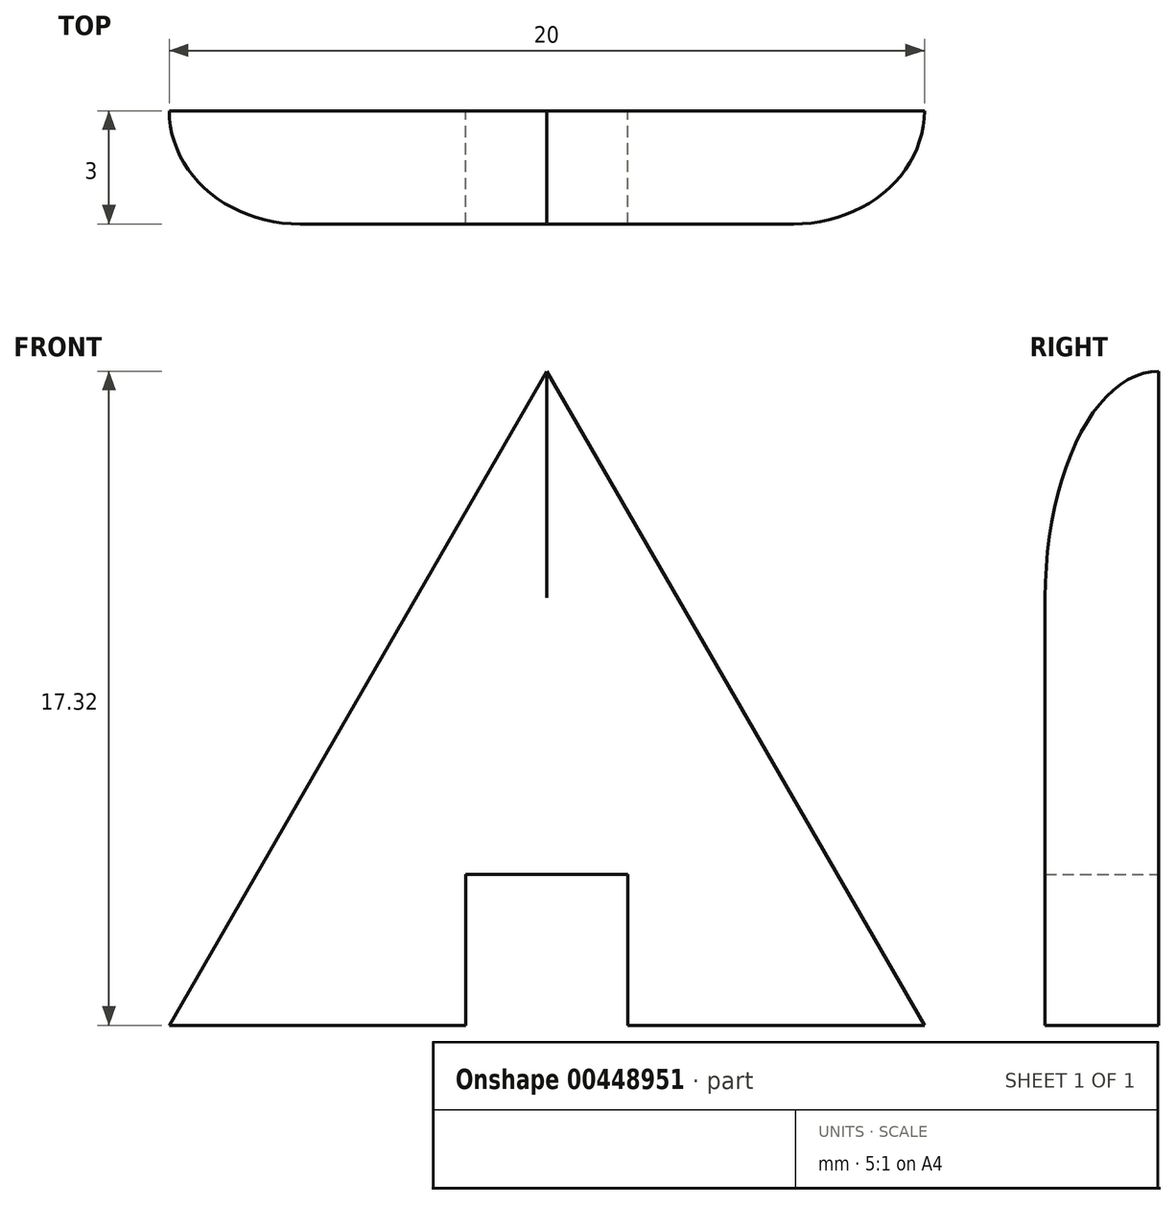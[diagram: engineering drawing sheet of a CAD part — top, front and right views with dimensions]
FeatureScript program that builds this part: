
annotation { "Feature Type Name" : "Feature", "Feature Type Description" : "" }
export const myFeature = defineFeature(function(context is Context, id is Id, definition is map)
    precondition{}
    {
        {
            var Q0;
            Q0=qCreatedBy(makeId("Front.planeOp"),FACE);
            var sketch = newSketch(context, id + "F0", { "sketchPlane" : qUnion([Q0])});
            skLineSegment(sketch, "E0", {"start": v(-10, 0) * mm, "end": v(-2.15, 0) * mm});
            skLineSegment(sketch, "E1", {"start": v(10, 0) * mm, "end": v(0, 17.32) * mm});
            skLineSegment(sketch, "E2", {"start": v(0, 17.32) * mm, "end": v(-10, 0) * mm});
            skLineSegment(sketch, "E3.top", {"start": v(-2.15, 4) * mm, "end": v(2.15, 4) * mm});
            skLineSegment(sketch, "E3.left", {"start": v(-2.15, 0) * mm, "end": v(-2.15, 4) * mm});
            skLineSegment(sketch, "E3.right", {"start": v(2.15, 0) * mm, "end": v(2.15, 4) * mm});
            skLineSegment(sketch, "E4.trimOffspring", {"start": v(2.15, 0) * mm, "end": v(10, 0) * mm});
            skSolve(sketch);
        }
        {
            var Q0;
            Q0 = qSketchRegion(id + "F0", true);
            extrude(context, id + "F1", {"entities" : qUnion([Q0]), "depth" : 3 * mm});
        }
        {
            var Q0;
            Q0=makeQuery(id+"F1.opExtrude","CAP_EDGE",EDGE,{"disambiguationData":[OSD([sQuery(id+"F0.wireOp",EDGE,"E2")])],"isStart":false});
            var Q1;
            Q1=makeQuery(id+"F1.opExtrude","CAP_EDGE",EDGE,{"disambiguationData":[OSD([sQuery(id+"F0.wireOp",EDGE,"E1")])],"isStart":false});
            fillet(context, id + "F2", {"entities" : qUnion([Q0, Q1]), "radius" : 3 * mm, "tangentPropagation" : true, "allowEdgeOverflow" : false});
        }
    });
